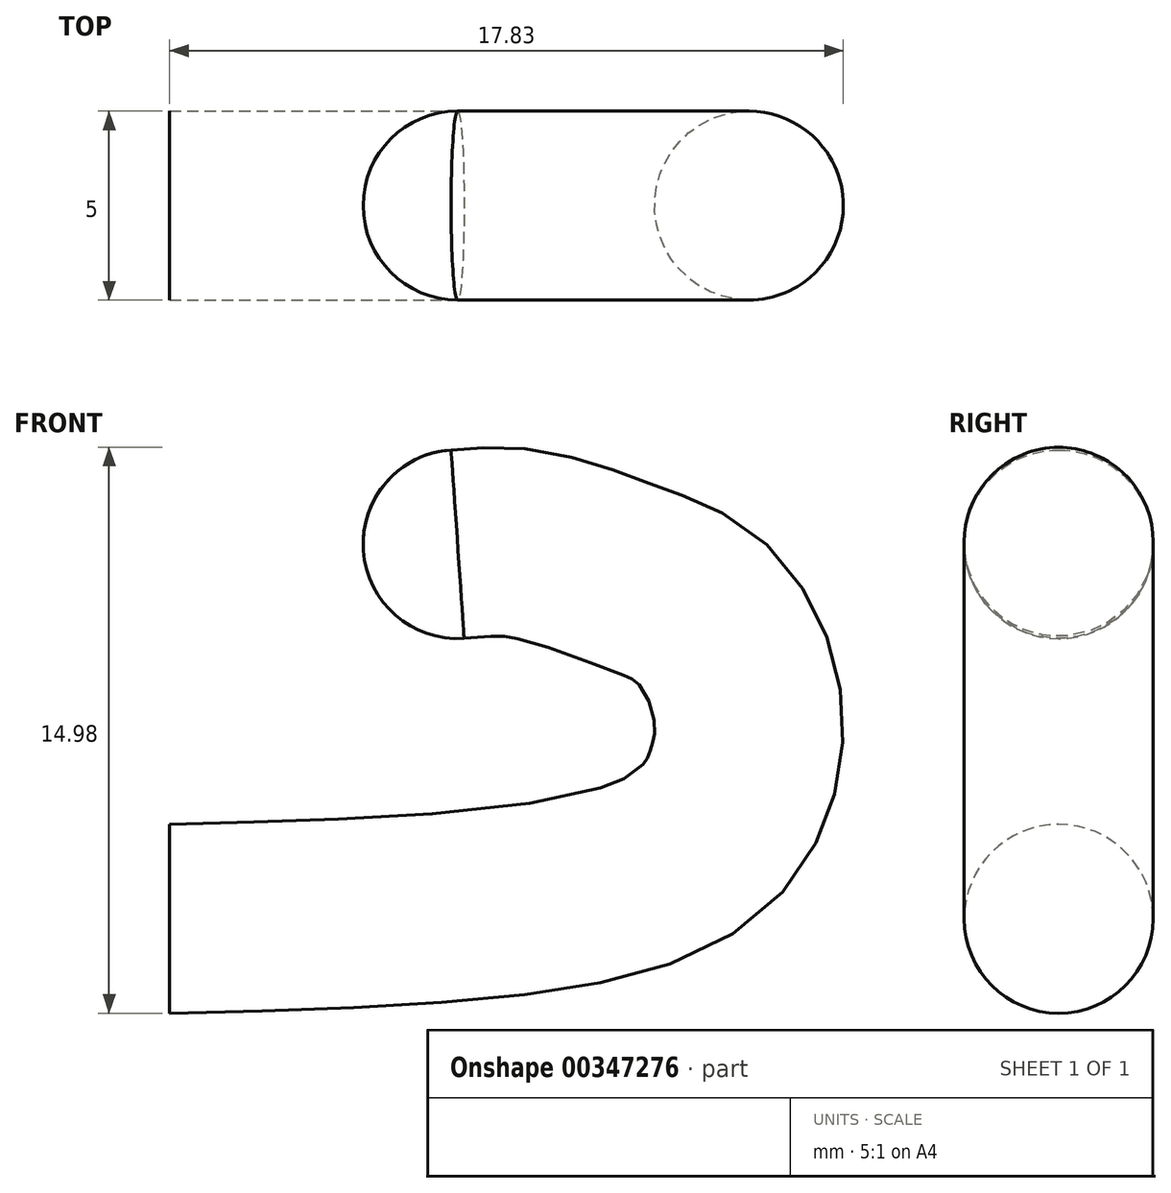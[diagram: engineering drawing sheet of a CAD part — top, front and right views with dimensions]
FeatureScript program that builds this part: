
annotation { "Feature Type Name" : "Feature", "Feature Type Description" : "" }
export const myFeature = defineFeature(function(context is Context, id is Id, definition is map)
    precondition{}
    {
        {
            var Q0;
            Q0=qCreatedBy(makeId("Right.planeOp"),FACE);
            var sketch = newSketch(context, id + "F0", { "sketchPlane" : qUnion([Q0])});
            skCircle(sketch, "E0", {"center": v(0, 0) * mm, "radius": 2.5 * mm});
            skSolve(sketch);
        }
        {
            var Q0;
            Q0=qCreatedBy(makeId("Front.planeOp"),FACE);
            var sketch = newSketch(context, id + "F1", { "sketchPlane" : qUnion([Q0])});
            skFitSpline(sketch, "E1", {"points": [v(0, 0) * mm, v(12.97, 1.39) * mm, v(15.06, 3.57) * mm, v(15.24, 5.93) * mm, v(14.06, 8.1) * mm, v(12.07, 9.1) * mm, v(9.43, 9.92) * mm, v(7.62, 9.92) * mm], "startDerivative": vector(56.36, 1.34) * mm, "endDerivative": vector(-16.58, -1.55) * mm});
            skSolve(sketch);
        }
        {
            var Q0;
            Q0=makeQuery(id+"F0.imprint","IMPRINT",FACE,{"disambiguationData":[TD([[makeQuery(id+"F0.imprint","IMPRINT",EDGE,{"derivedFrom":sQuery(id+"F0.wireOp",EDGE,"E0")}),1.0]])]});
            var Q1;
            Q1=sQuery(id+"F1.wireOp",EDGE,"E1");
            sweep(context, id + "F2", {"profiles" : qUnion([Q0]), "path" : qUnion([Q1])});
        }
        {
            var Q0;
            Q0=makeQuery(id+"F2.opSweep","CAP_FACE",FACE,{"disambiguationData":[OSD([sQuery(id+"F0.wireOp",EDGE,"E0"),sQuery(id+"F1.wireOp",VERTEX,"E1.end")])],"isStart":false});
            extrude(context, id + "F3", {"entities" : qUnion([Q0]), "operationType" : NewBodyOperationType.ADD, "depth" : 2.5 * mm});
        }
        {
            var Q0;
            Q0=makeQuery(id+"F3.opExtrude","CAP_EDGE",EDGE,{"disambiguationData":[OSD([sQuery(id+"F0.wireOp",EDGE,"E0"),sQuery(id+"F1.wireOp",VERTEX,"E1.end")])],"isStart":false});
            fillet(context, id + "F4", {"entities" : qUnion([Q0]), "radius" : 2.5 * mm, "tangentPropagation" : true, "allowEdgeOverflow" : false});
        }
    });
